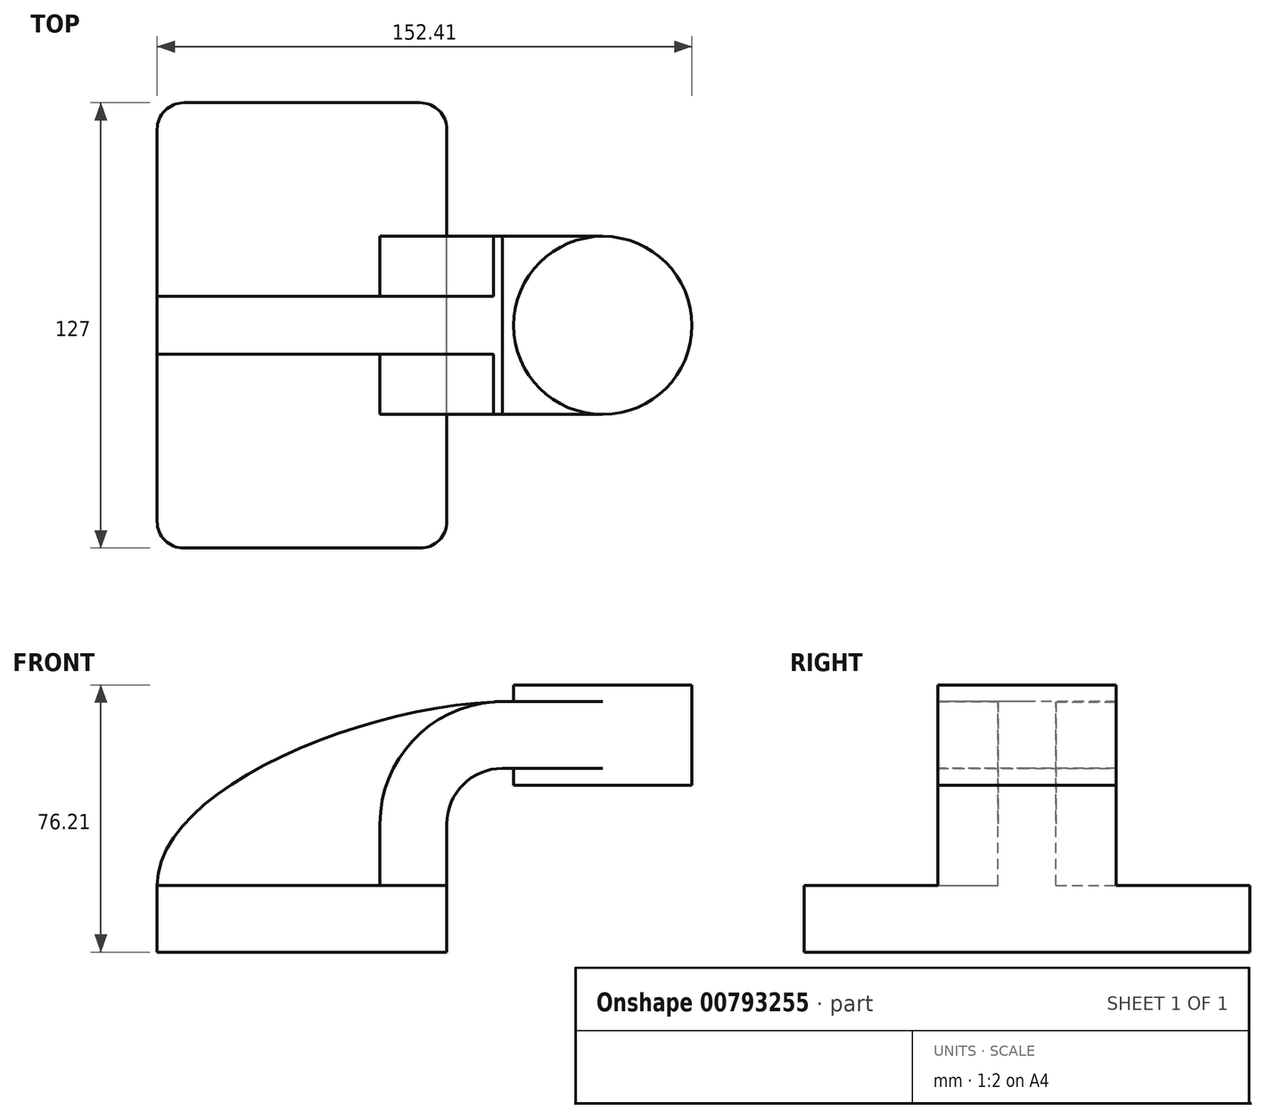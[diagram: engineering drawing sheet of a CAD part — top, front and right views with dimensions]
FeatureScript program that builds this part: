
annotation { "Feature Type Name" : "Feature", "Feature Type Description" : "" }
export const myFeature = defineFeature(function(context is Context, id is Id, definition is map)
    precondition{}
    {
        {
            var Q0;
            Q0=qCreatedBy(makeId("Front.planeOp"),FACE);
            var sketch = newSketch(context, id + "F0", { "sketchPlane" : qUnion([Q0])});
            skLineSegment(sketch, "E0.bottom", {"start": v(41.28, -9.52) * mm, "end": v(-41.28, -9.53) * mm});
            skLineSegment(sketch, "E0.top", {"start": v(41.28, 9.52) * mm, "end": v(-41.28, 9.52) * mm});
            skLineSegment(sketch, "E0.left", {"start": v(41.28, -9.53) * mm, "end": v(41.27, 9.52) * mm});
            skLineSegment(sketch, "E0.right", {"start": v(-41.27, -9.53) * mm, "end": v(-41.28, 9.52) * mm});
            skPoint(sketch, "E0.middle", {"position": v(0, 0) * mm});
            skLineSegment(sketch, "E1.bottom", {"start": v(111.12, 38.1) * mm, "end": v(60.33, 38.1) * mm});
            skLineSegment(sketch, "E1.top", {"start": v(111.12, 66.67) * mm, "end": v(60.33, 66.67) * mm});
            skLineSegment(sketch, "E1.left", {"start": v(111.13, 38.1) * mm, "end": v(111.13, 66.67) * mm});
            skLineSegment(sketch, "E1.right", {"start": v(60.33, 38.1) * mm, "end": v(60.32, 66.67) * mm});
            skPoint(sketch, "E1.middle", {"position": v(85.73, 52.39) * mm});
            skLineSegment(sketch, "E2", {"start": v(41.28, 9.53) * mm, "end": v(41.28, 27) * mm});
            skArc(sketch, "E3", {"start": v(57.15, 42.88) * mm, "mid": v(45.92, 38.23) * mm, "end": v(41.28, 27) * mm});
            skLineSegment(sketch, "E4", {"start": v(57.15, 42.88) * mm, "end": v(85.73, 42.88) * mm});
            skPoint(sketch, "E4.endSnap0", {"position": v(85.73, 38.1) * mm});
            skLineSegment(sketch, "E5.0", {"start": v(57.15, 61.93) * mm, "end": v(85.73, 61.93) * mm});
            skArc(sketch, "E5.1", {"start": v(57.15, 61.93) * mm, "mid": v(32.45, 51.7) * mm, "end": v(22.23, 27) * mm});
            skLineSegment(sketch, "E5.2", {"start": v(22.23, 9.53) * mm, "end": v(22.23, 27) * mm});
            skLineSegment(sketch, "E6", {"start": v(85.72, 38.1) * mm, "end": v(85.72, 66.67) * mm});
            skFitSpline(sketch, "E7", {"points": [v(-41.28, 9.52) * mm, v(57.15, 61.93) * mm], "startDerivative": vector(-0.1, 81.76) * mm, "endDerivative": vector(120.6, 2.99) * mm});
            skSolve(sketch);
        }
        {
            var Q0;
            Q0=makeQuery(id+"F0.imprint","IMPRINT",FACE,{"disambiguationData":[TD([[makeQuery(id+"F0.imprint","IMPRINT",EDGE,{"derivedFrom":sQuery(id+"F0.wireOp",EDGE,"E0.bottom")}),-1.0]])]});
            extrude(context, id + "F1", {"entities" : qUnion([Q0]), "endBound" : BoundingType.SYMMETRIC, "depth" : 127 * mm, "offsetDistance" : 25.4 * mm});
        }
        {
            var Q0;
            {var subQ1=sQuery(id+"F0.wireOp",EDGE,"E2");Q0=makeQuery(id+"F0.imprint","IMPRINT",FACE,{"disambiguationData":[TD([[makeQuery(id+"F0.imprint","IMPRINT",EDGE,{"derivedFrom":subQ1}),1.0]])]});}
            var Q1;
            {var subQ0=sQuery(id+"F0.wireOp",EDGE,"E4");var subQ1=sQuery(id+"F0.wireOp",EDGE,"E1.right");var subQ2=makeQuery(id+"F0.imprint","INTERSECT",VERTEX,{"derivedFrom":[subQ1,subQ0]});Q1=makeQuery(id+"F0.imprint","IMPRINT",FACE,{"disambiguationData":[TD([[makeQuery(id+"F0.imprint","IMPRINT",EDGE,{"disambiguationData":[TD([[subQ2,-1.0]])],"derivedFrom":subQ1}),-1.0]])]});}
            extrude(context, id + "F2", {"entities" : qUnion([Q0, Q1]), "operationType" : NewBodyOperationType.ADD, "endBound" : BoundingType.SYMMETRIC, "depth" : 50.8 * mm, "offsetDistance" : 25.4 * mm});
        }
        {
            var Q0;
            {var subQ3=sQuery(id+"F0.wireOp",EDGE,"E5.2");Q0=makeQuery(id+"F0.imprint","IMPRINT",FACE,{"disambiguationData":[TD([[makeQuery(id+"F0.imprint","IMPRINT",EDGE,{"derivedFrom":subQ3}),1.0]])]});}
            extrude(context, id + "F3", {"entities" : qUnion([Q0]), "operationType" : NewBodyOperationType.ADD, "endBound" : BoundingType.SYMMETRIC, "depth" : 16.5 * mm, "offsetDistance" : 25.4 * mm});
        }
        {
            var Q0;
            {var subQ0=sQuery(id+"F0.wireOp",EDGE,"E1.left");Q0=makeQuery(id+"F0.imprint","IMPRINT",FACE,{"disambiguationData":[TD([[makeQuery(id+"F0.imprint","IMPRINT",EDGE,{"derivedFrom":subQ0}),1.0]])]});}
            var Q1;
            Q1=sQuery(id+"F0.wireOp",EDGE,"E6");
            revolve(context, id + "F4", {"operationType" : NewBodyOperationType.ADD, "surfaceOperationType" : NewSurfaceOperationType.NEW, "entities" : qUnion([Q0]), "axis" : qUnion([Q1]), "revolveType" : RevolveType.FULL});
        }
        {
            var Q0;
            Q0=makeQuery(id+"F1.opExtrude","CAP_EDGE",EDGE,{"disambiguationData":[OSD([sQuery(id+"F0.wireOp",EDGE,"E0.right")])],"isStart":false});
            var Q1;
            Q1=makeQuery(id+"F1.opExtrude","CAP_EDGE",EDGE,{"disambiguationData":[OSD([sQuery(id+"F0.wireOp",EDGE,"E0.left")])],"isStart":false});
            var Q2;
            Q2=makeQuery(id+"F1.opExtrude","CAP_EDGE",EDGE,{"disambiguationData":[OSD([sQuery(id+"F0.wireOp",EDGE,"E0.left")])],"isStart":true});
            var Q3;
            Q3=makeQuery(id+"F1.opExtrude","CAP_EDGE",EDGE,{"disambiguationData":[OSD([sQuery(id+"F0.wireOp",EDGE,"E0.right")])],"isStart":true});
            fillet(context, id + "F5", {"entities" : qUnion([Q0, Q1, Q2, Q3]), "radius" : 7.62 * mm, "tangentPropagation" : true, "allowEdgeOverflow" : false});
        }
    });
